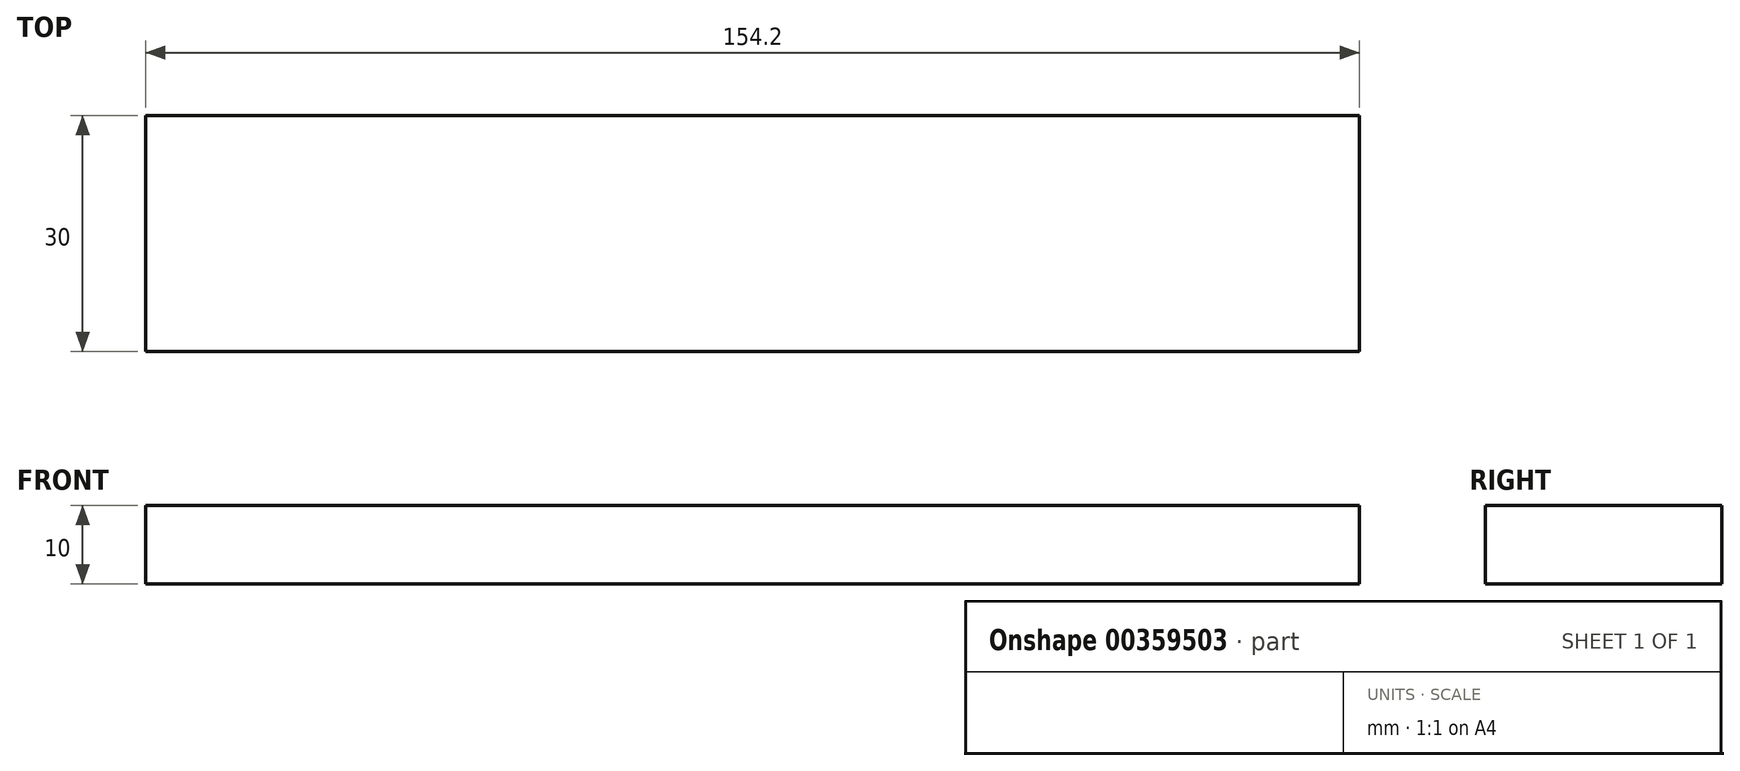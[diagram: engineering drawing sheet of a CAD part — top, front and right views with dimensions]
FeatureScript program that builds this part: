
annotation { "Feature Type Name" : "Feature", "Feature Type Description" : "" }
export const myFeature = defineFeature(function(context is Context, id is Id, definition is map)
    precondition{}
    {
        {
            var Q0;
            Q0=qCreatedBy(makeId("Top.planeOp"),FACE);
            var sketch = newSketch(context, id + "F0", { "sketchPlane" : qUnion([Q0])});
            skLineSegment(sketch, "E0.bottom", {"start": v(-77.72, -5.6) * mm, "end": v(76.48, -5.6) * mm});
            skLineSegment(sketch, "E0.top", {"start": v(-77.72, -35.6) * mm, "end": v(76.48, -35.6) * mm});
            skLineSegment(sketch, "E0.left", {"start": v(-77.72, -5.6) * mm, "end": v(-77.72, -35.6) * mm});
            skLineSegment(sketch, "E0.right", {"start": v(76.48, -5.6) * mm, "end": v(76.48, -35.6) * mm});
            skSolve(sketch);
        }
        {
            var Q0;
            Q0=makeQuery(id+"F0.imprint","IMPRINT",FACE,{"disambiguationData":[TD([[makeQuery(id+"F0.imprint","IMPRINT",EDGE,{"derivedFrom":sQuery(id+"F0.wireOp",EDGE,"E0.bottom")}),-1.0]])]});
            extrude(context, id + "F1", {"entities" : qUnion([Q0]), "depth" : 10 * mm});
        }
    });
